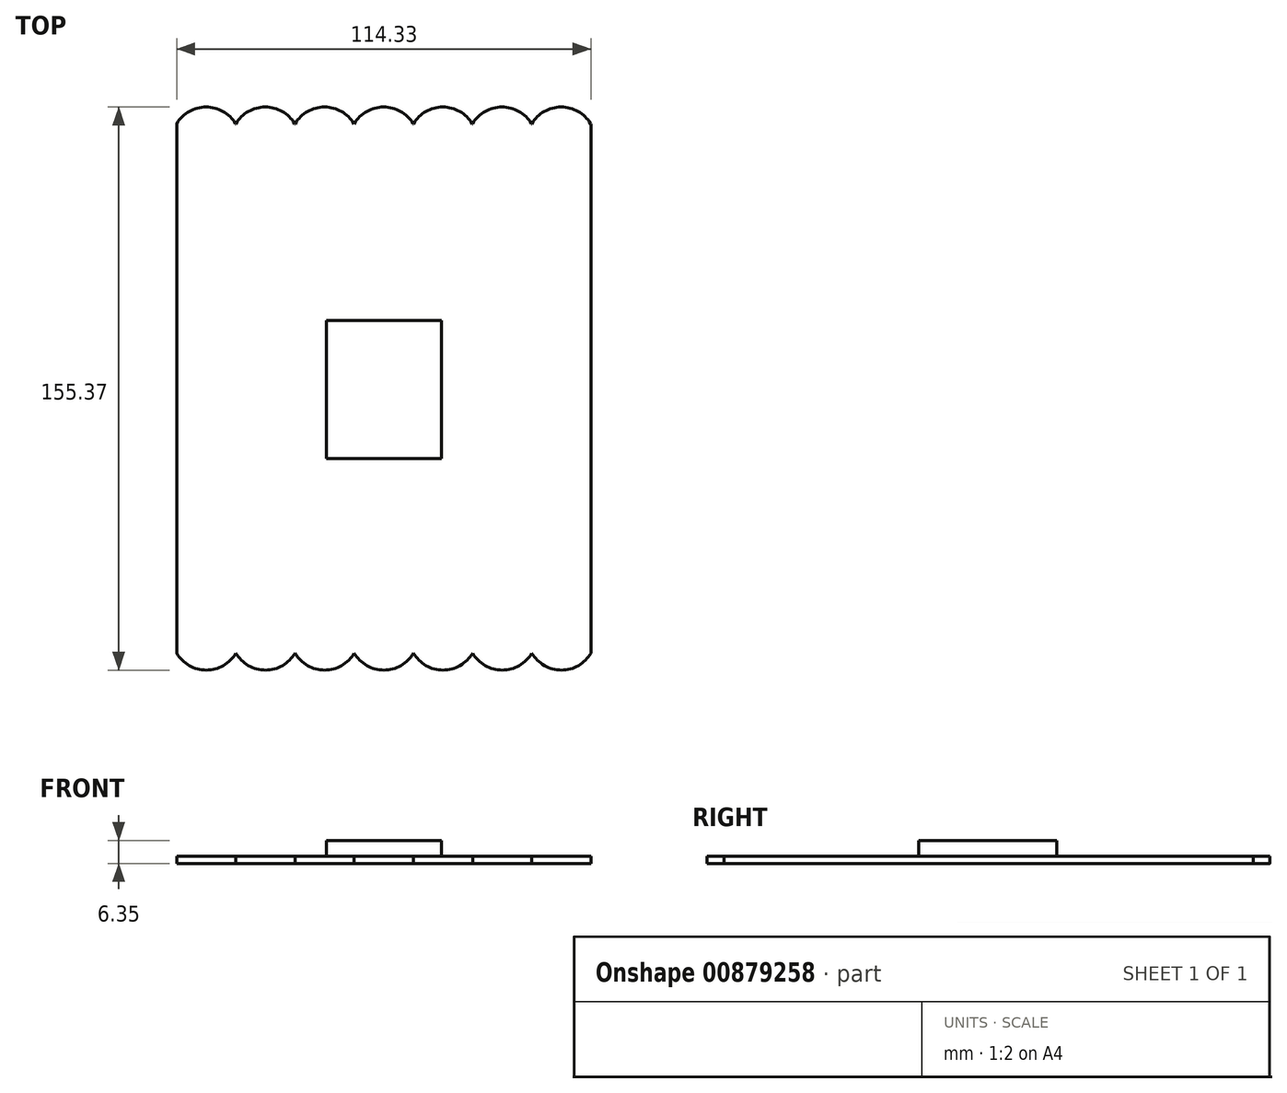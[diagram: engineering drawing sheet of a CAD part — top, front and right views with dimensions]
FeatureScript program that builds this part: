
annotation { "Feature Type Name" : "Feature", "Feature Type Description" : "" }
export const myFeature = defineFeature(function(context is Context, id is Id, definition is map)
    precondition{}
    {
        {
            var Q0;
            Q0=qCreatedBy(makeId("Top.planeOp"),FACE);
            var sketch = newSketch(context, id + "F0", { "sketchPlane" : qUnion([Q0])});
            skLineSegment(sketch, "E0.bottom", {"start": v(-25.77, 110.77) * mm, "end": v(-25.67, 110.77) * mm});
            skLineSegment(sketch, "E0.left", {"start": v(-42, 110.77) * mm, "end": v(-42, -35.28) * mm});
            skLineSegment(sketch, "E0.right", {"start": v(72.3, 110.77) * mm, "end": v(72.3, -35.28) * mm});
            skArc(sketch, "E1", {"start": v(-25.77, 110.77) * mm, "mid": v(-33.88, 115.4) * mm, "end": v(-42, 110.77) * mm});
            skArc(sketch, "E2.1.0.0", {"start": v(-9.44, 110.77) * mm, "mid": v(-17.55, 115.4) * mm, "end": v(-25.67, 110.77) * mm});
            skArc(sketch, "E2.2.0.0", {"start": v(6.9, 110.77) * mm, "mid": v(-1.22, 115.39) * mm, "end": v(-9.33, 110.77) * mm});
            skArc(sketch, "E2.3.0.0", {"start": v(23.23, 110.77) * mm, "mid": v(15.11, 115.39) * mm, "end": v(7, 110.77) * mm});
            skArc(sketch, "E2.4.0.0", {"start": v(39.56, 110.77) * mm, "mid": v(31.45, 115.39) * mm, "end": v(23.33, 110.77) * mm});
            skArc(sketch, "E2.5.0.0", {"start": v(55.89, 110.77) * mm, "mid": v(47.78, 115.38) * mm, "end": v(39.67, 110.77) * mm});
            skArc(sketch, "E2.6.0.0", {"start": v(72.23, 110.76) * mm, "mid": v(64.11, 115.38) * mm, "end": v(56, 110.77) * mm});
            skLineSegment(sketch, "E3.trimOffspring", {"start": v(72.22, 110.77) * mm, "end": v(72.3, 110.77) * mm});
            skLineSegment(sketch, "E4.trimOffspring", {"start": v(55.89, 110.77) * mm, "end": v(56, 110.77) * mm});
            skLineSegment(sketch, "E5.trimOffspring", {"start": v(39.56, 110.77) * mm, "end": v(39.67, 110.77) * mm});
            skLineSegment(sketch, "E6.trimOffspring", {"start": v(23.23, 110.77) * mm, "end": v(23.33, 110.77) * mm});
            skLineSegment(sketch, "E7.trimOffspring", {"start": v(6.9, 110.77) * mm, "end": v(7, 110.77) * mm});
            skLineSegment(sketch, "E8.trimOffspring", {"start": v(-9.44, 110.77) * mm, "end": v(-9.33, 110.77) * mm});
            skArc(sketch, "E9", {"start": v(-42, -35.28) * mm, "mid": v(-33.83, -39.98) * mm, "end": v(-25.67, -35.28) * mm});
            skArc(sketch, "E10.1.0.0", {"start": v(-25.67, -35.28) * mm, "mid": v(-17.5, -39.98) * mm, "end": v(-9.33, -35.28) * mm});
            skArc(sketch, "E10.2.0.0", {"start": v(-9.33, -35.28) * mm, "mid": v(-1.17, -39.98) * mm, "end": v(7, -35.28) * mm});
            skArc(sketch, "E10.3.0.0", {"start": v(7, -35.28) * mm, "mid": v(15.17, -39.98) * mm, "end": v(23.33, -35.28) * mm});
            skArc(sketch, "E10.4.0.0", {"start": v(23.33, -35.28) * mm, "mid": v(31.5, -39.98) * mm, "end": v(39.67, -35.28) * mm});
            skArc(sketch, "E10.5.0.0", {"start": v(39.67, -35.28) * mm, "mid": v(47.83, -39.98) * mm, "end": v(56, -35.28) * mm});
            skArc(sketch, "E10.6.0.0", {"start": v(56, -35.28) * mm, "mid": v(64.17, -39.98) * mm, "end": v(72.33, -35.28) * mm});
            skLineSegment(sketch, "E11", {"start": v(-25.67, -35.28) * mm, "end": v(-25.67, -35.28) * mm});
            skLineSegment(sketch, "E12", {"start": v(-9.33, -35.28) * mm, "end": v(-9.33, -35.28) * mm});
            skLineSegment(sketch, "E13", {"start": v(7, -35.28) * mm, "end": v(7, -35.28) * mm});
            skLineSegment(sketch, "E14", {"start": v(39.67, -35.28) * mm, "end": v(39.67, -35.28) * mm});
            skLineSegment(sketch, "E15", {"start": v(72.33, -35.28) * mm, "end": v(72.3, -35.28) * mm});
            skPoint(sketch, "E16.end.orphan", {"position": v(72.23, 37.75) * mm});
            skPoint(sketch, "E16.start.orphan", {"position": v(-42, 37.75) * mm});
            skLineSegment(sketch, "E17", {"start": v(56, -35.28) * mm, "end": v(56, -35.28) * mm});
            skLineSegment(sketch, "E18", {"start": v(23.33, -35.28) * mm, "end": v(23.33, -35.28) * mm});
            skSolve(sketch);
        }
        {
            var Q0;
            Q0=qCreatedBy(makeId("Top.planeOp"),FACE);
            var sketch = newSketch(context, id + "F1", { "sketchPlane" : qUnion([Q0])});
            skLineSegment(sketch, "E19", {"start": v(31.04, 56.55) * mm, "end": v(-0.7, 56.55) * mm});
            skLineSegment(sketch, "E20", {"start": v(-0.7, 56.55) * mm, "end": v(-0.7, 18.45) * mm});
            skLineSegment(sketch, "E21", {"start": v(-0.7, 18.45) * mm, "end": v(31.04, 18.45) * mm});
            skLineSegment(sketch, "E22", {"start": v(31.04, 18.45) * mm, "end": v(31.04, 56.55) * mm});
            skSolve(sketch);
        }
        {
            var Q0;
            {var subQ5=sQuery(id+"F0.wireOp",EDGE,"E0.bottom");Q0=makeQuery(id+"F0.imprint","IMPRINT",FACE,{"disambiguationData":[TD([[makeQuery(id+"F0.imprint","IMPRINT",EDGE,{"derivedFrom":subQ5}),-1.0]])]});}
            extrude(context, id + "F2", {"entities" : qUnion([Q0]), "depth" : 2.03 * mm, "offsetDistance" : 25.4 * mm});
        }
        {
            var Q0;
            Q0=makeQuery(id+"F1.imprint","IMPRINT",FACE,{"disambiguationData":[TD([[makeQuery(id+"F1.imprint","IMPRINT",EDGE,{"derivedFrom":sQuery(id+"F1.wireOp",EDGE,"E19")}),1.0]])]});
            extrude(context, id + "F3", {"entities" : qUnion([Q0]), "operationType" : NewBodyOperationType.ADD, "depth" : 6.35 * mm, "offsetDistance" : 25.4 * mm});
        }
    });
